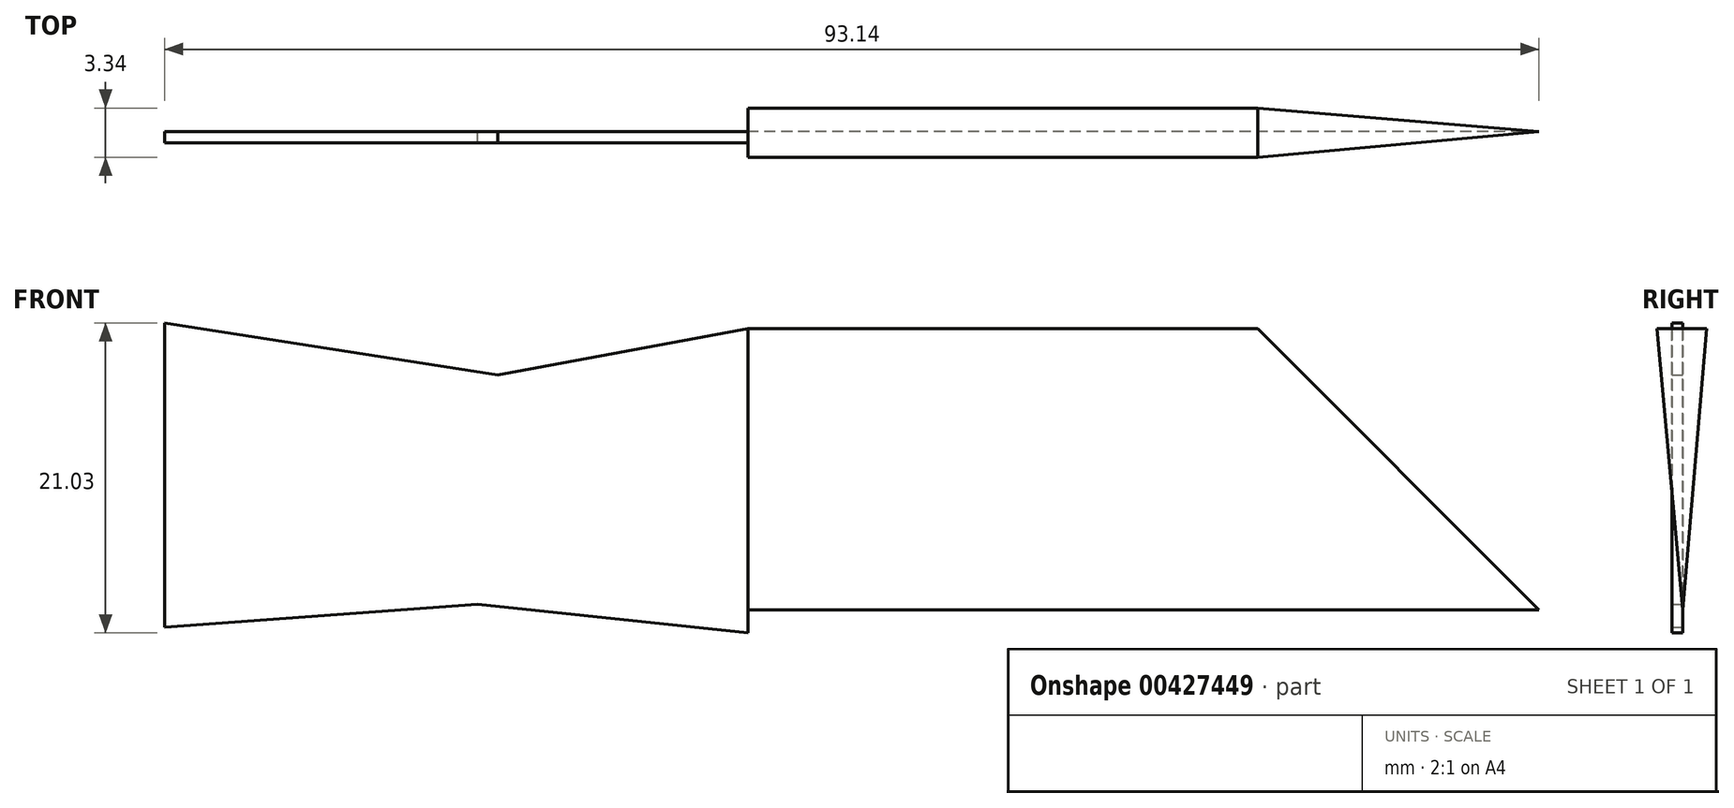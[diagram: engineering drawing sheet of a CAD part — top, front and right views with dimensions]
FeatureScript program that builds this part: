
annotation { "Feature Type Name" : "Feature", "Feature Type Description" : "" }
export const myFeature = defineFeature(function(context is Context, id is Id, definition is map)
    precondition{}
    {
        {
            var Q0;
            Q0=qCreatedBy(makeId("Right.planeOp"),FACE);
            var sketch = newSketch(context, id + "F0", { "sketchPlane" : qUnion([Q0])});
            skLineSegment(sketch, "E0", {"start": v(0, 10.7) * mm, "end": v(1.59, 10.7) * mm});
            skLineSegment(sketch, "E1", {"start": v(1.59, 10.7) * mm, "end": v(0, -8.37) * mm});
            skLineSegment(sketch, "E2", {"start": v(0, 10.7) * mm, "end": v(-1.75, 10.7) * mm});
            skLineSegment(sketch, "E3", {"start": v(-1.75, 10.7) * mm, "end": v(0, -8.37) * mm});
            skSolve(sketch);
        }
        {
            var Q0;
            Q0=makeQuery(id+"F0.imprint","IMPRINT",FACE,{"disambiguationData":[TD([[makeQuery(id+"F0.imprint","IMPRINT",EDGE,{"derivedFrom":sQuery(id+"F0.wireOp",EDGE,"E0")}),-1.0]])]});
            extrude(context, id + "F1", {"entities" : qUnion([Q0]), "depth" : 59.94 * mm});
        }
        {
            var Q0;
            Q0=makeQuery(id+"F1.opExtrude","CAP_EDGE",EDGE,{"disambiguationData":[OSD([sQuery(id+"F0.wireOp",EDGE,"E0"),sQuery(id+"F0.wireOp",EDGE,"E2")])],"isStart":false});
            chamfer(context, id + "F2", {"entities" : qUnion([Q0]), "width" : 25.4 * mm, "tangentPropagation" : true});
        }
        {
            var Q0;
            Q0=qCreatedBy(makeId("Front.planeOp"),FACE);
            var sketch = newSketch(context, id + "F3", { "sketchPlane" : qUnion([Q0])});
            skLineSegment(sketch, "E4", {"start": v(0, 10.7) * mm, "end": v(0, -9.93) * mm});
            skLineSegment(sketch, "E5", {"start": v(0, -9.93) * mm, "end": v(-18.3, -7.98) * mm});
            skLineSegment(sketch, "E6", {"start": v(-18.3, -7.98) * mm, "end": v(-39.52, -9.54) * mm});
            skLineSegment(sketch, "E7", {"start": v(-39.52, -9.54) * mm, "end": v(-39.52, 11.1) * mm});
            skLineSegment(sketch, "E8", {"start": v(-39.52, 11.1) * mm, "end": v(-16.94, 7.6) * mm});
            skLineSegment(sketch, "E9", {"start": v(-16.94, 7.6) * mm, "end": v(0, 10.7) * mm});
            skSolve(sketch);
        }
        {
            var Q0;
            Q0=makeQuery(id+"F3.imprint","IMPRINT",FACE,{"disambiguationData":[TD([[makeQuery(id+"F3.imprint","IMPRINT",EDGE,{"derivedFrom":sQuery(id+"F3.wireOp",EDGE,"E4")}),-1.0]])]});
            extrude(context, id + "F4", {"entities" : qUnion([Q0]), "operationType" : NewBodyOperationType.ADD, "depth" : 0.76 * mm});
        }
    });
